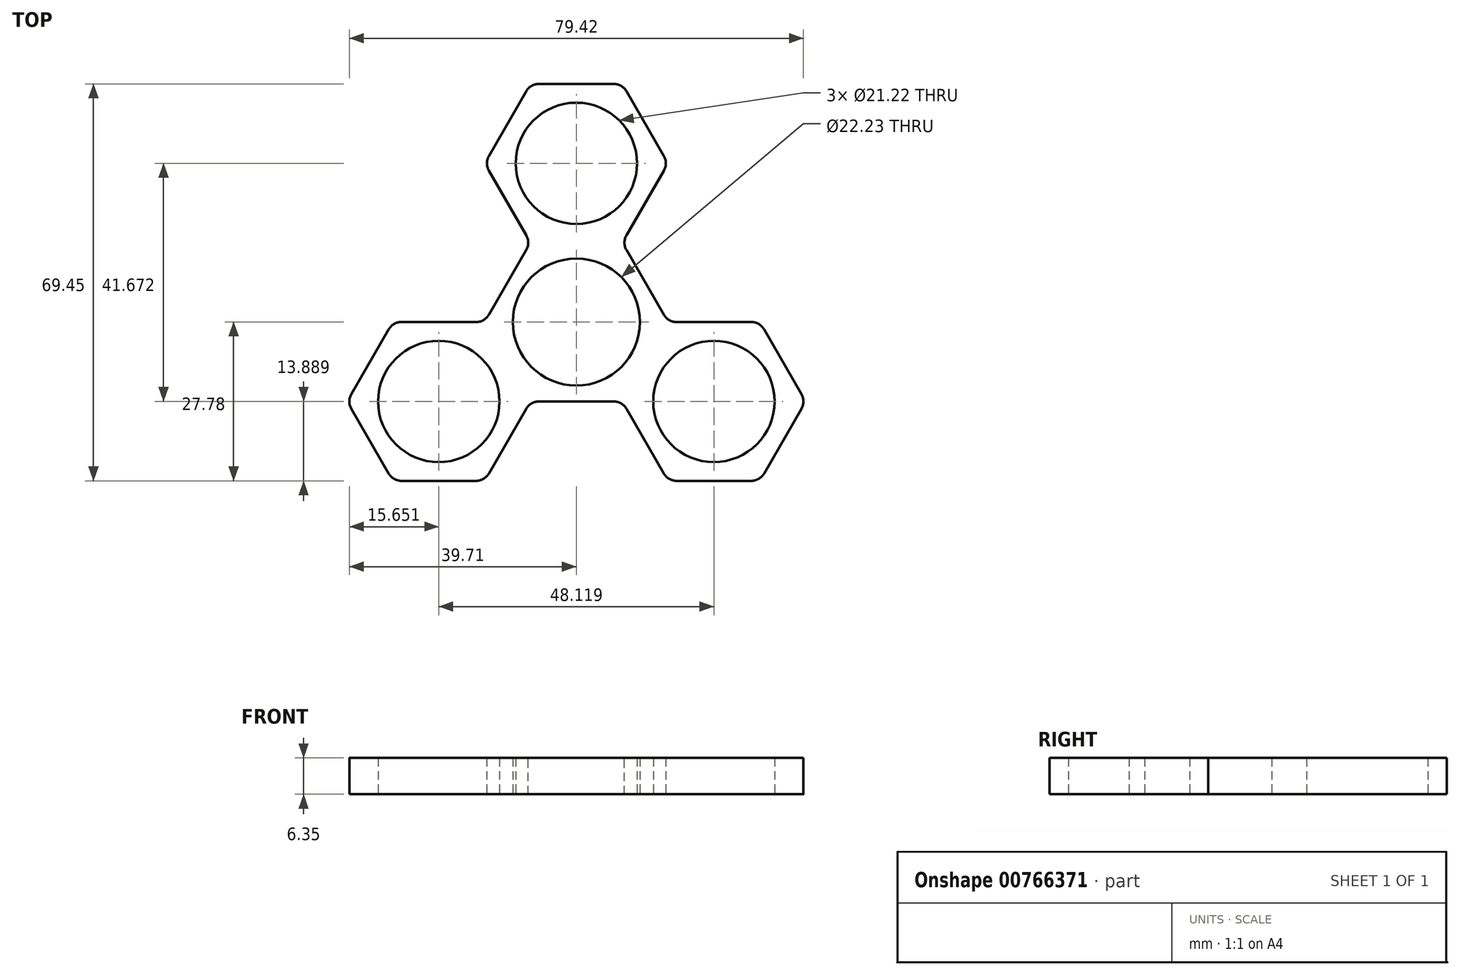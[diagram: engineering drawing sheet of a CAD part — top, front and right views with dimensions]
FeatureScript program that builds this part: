
annotation { "Feature Type Name" : "Feature", "Feature Type Description" : "" }
export const myFeature = defineFeature(function(context is Context, id is Id, definition is map)
    precondition{}
    {
        {
            var Q0;
            Q0=qCreatedBy(makeId("Top.planeOp"),FACE);
            var sketch = newSketch(context, id + "F0", { "sketchPlane" : qUnion([Q0])});
            skCircle(sketch, "E0", {"center": v(0, 0) * mm, "radius": 13.9 * mm});
            skCircle(sketch, "E1.cCircle", {"center": v(0, 0) * mm, "radius": 13.9 * mm, "construction": true});
            skLineSegment(sketch, "E1.0", {"start": v(-8.02, 13.9) * mm, "end": v(8.02, 13.9) * mm});
            skLineSegment(sketch, "E1.1", {"start": v(8.02, 13.9) * mm, "end": v(16.04, 0) * mm});
            skLineSegment(sketch, "E1.2", {"start": v(16.04, 0) * mm, "end": v(8.02, -13.9) * mm});
            skLineSegment(sketch, "E1.3", {"start": v(8.02, -13.9) * mm, "end": v(-8.02, -13.9) * mm});
            skLineSegment(sketch, "E1.4", {"start": v(-8.02, -13.9) * mm, "end": v(-16.04, 0) * mm});
            skLineSegment(sketch, "E1.5", {"start": v(-16.04, 0) * mm, "end": v(-8.02, 13.9) * mm});
            skPoint(sketch, "E1.0.midPoint", {"position": v(0, 13.9) * mm});
            skCircle(sketch, "E2", {"center": v(0, 27.78) * mm, "radius": 13.9 * mm});
            skLineSegment(sketch, "E3.0", {"start": v(8.02, 13.9) * mm, "end": v(-8.02, 13.9) * mm});
            skLineSegment(sketch, "E3.1", {"start": v(-8.02, 13.9) * mm, "end": v(-16.04, 27.78) * mm});
            skLineSegment(sketch, "E3.2", {"start": v(-16.04, 27.78) * mm, "end": v(-8.02, 41.67) * mm});
            skLineSegment(sketch, "E3.3", {"start": v(-8.02, 41.67) * mm, "end": v(8.02, 41.67) * mm});
            skLineSegment(sketch, "E3.4", {"start": v(8.02, 41.67) * mm, "end": v(16.04, 27.78) * mm});
            skLineSegment(sketch, "E3.5", {"start": v(16.04, 27.78) * mm, "end": v(8.02, 13.9) * mm});
            skCircle(sketch, "E4.cCircle", {"center": v(-24.06, -13.9) * mm, "radius": 13.9 * mm, "construction": true});
            skLineSegment(sketch, "E4.0", {"start": v(-16.04, 0) * mm, "end": v(-8.02, -13.9) * mm});
            skLineSegment(sketch, "E4.1", {"start": v(-8.02, -13.9) * mm, "end": v(-16.04, -27.78) * mm});
            skLineSegment(sketch, "E4.2", {"start": v(-16.04, -27.78) * mm, "end": v(-32.08, -27.78) * mm});
            skLineSegment(sketch, "E4.3", {"start": v(-32.08, -27.78) * mm, "end": v(-40.1, -13.9) * mm});
            skLineSegment(sketch, "E4.4", {"start": v(-40.1, -13.9) * mm, "end": v(-32.08, 0) * mm});
            skLineSegment(sketch, "E4.5", {"start": v(-32.08, 0) * mm, "end": v(-16.04, 0) * mm});
            skPoint(sketch, "E4.0.midPoint", {"position": v(-12.03, -6.95) * mm});
            skCircle(sketch, "E5.cCircle", {"center": v(24.06, -13.9) * mm, "radius": 13.9 * mm, "construction": true});
            skLineSegment(sketch, "E5.0", {"start": v(8.02, -13.9) * mm, "end": v(16.04, 0) * mm});
            skLineSegment(sketch, "E5.1", {"start": v(16.04, 0) * mm, "end": v(32.08, 0) * mm});
            skLineSegment(sketch, "E5.2", {"start": v(32.08, 0) * mm, "end": v(40.1, -13.9) * mm});
            skLineSegment(sketch, "E5.3", {"start": v(40.1, -13.9) * mm, "end": v(32.08, -27.78) * mm});
            skLineSegment(sketch, "E5.4", {"start": v(32.08, -27.78) * mm, "end": v(16.04, -27.78) * mm});
            skLineSegment(sketch, "E5.5", {"start": v(16.04, -27.78) * mm, "end": v(8.02, -13.9) * mm});
            skPoint(sketch, "E5.0.midPoint", {"position": v(12.03, -6.95) * mm});
            skCircle(sketch, "E6", {"center": v(-24.06, -13.9) * mm, "radius": 10.6 * mm});
            skCircle(sketch, "E7", {"center": v(0, 0) * mm, "radius": 11.11 * mm});
            skCircle(sketch, "E8", {"center": v(0, 27.78) * mm, "radius": 10.6 * mm});
            skCircle(sketch, "E9", {"center": v(24.06, -13.9) * mm, "radius": 10.6 * mm});
            skSolve(sketch);
        }
        {
            var Q0;
            Q0 = qSketchRegion(id + "F0", true);
            extrude(context, id + "F1", {"entities" : qUnion([Q0]), "depth" : 6.35 * mm, "offsetDistance" : 25.4 * mm});
        }
        {
            var Q0;
            Q0=makeQuery(id+"F1.opExtrude","SWEPT_EDGE",EDGE,{"disambiguationData":[OSD([sQuery(id+"F0.wireOp",EDGE,"E1.3"),sQuery(id+"F0.wireOp",EDGE,"E4.0"),sQuery(id+"F0.wireOp",EDGE,"E4.1")])]});
            var Q1;
            Q1=makeQuery(id+"F1.opExtrude","SWEPT_EDGE",EDGE,{"disambiguationData":[OSD([sQuery(id+"F0.wireOp",EDGE,"E1.3"),sQuery(id+"F0.wireOp",EDGE,"E5.0"),sQuery(id+"F0.wireOp",EDGE,"E5.5")])]});
            var Q2;
            Q2=makeQuery(id+"F1.opExtrude","SWEPT_EDGE",EDGE,{"disambiguationData":[OSD([sQuery(id+"F0.wireOp",EDGE,"E5.4"),sQuery(id+"F0.wireOp",EDGE,"E5.5")])]});
            var Q3;
            Q3=makeQuery(id+"F1.opExtrude","SWEPT_EDGE",EDGE,{"disambiguationData":[OSD([sQuery(id+"F0.wireOp",EDGE,"E5.3"),sQuery(id+"F0.wireOp",EDGE,"E5.4")])]});
            var Q4;
            Q4=makeQuery(id+"F1.opExtrude","SWEPT_EDGE",EDGE,{"disambiguationData":[OSD([sQuery(id+"F0.wireOp",EDGE,"E5.2"),sQuery(id+"F0.wireOp",EDGE,"E5.3")])]});
            var Q5;
            Q5=makeQuery(id+"F1.opExtrude","SWEPT_EDGE",EDGE,{"disambiguationData":[OSD([sQuery(id+"F0.wireOp",EDGE,"E4.1"),sQuery(id+"F0.wireOp",EDGE,"E4.2")])]});
            var Q6;
            Q6=makeQuery(id+"F1.opExtrude","SWEPT_EDGE",EDGE,{"disambiguationData":[OSD([sQuery(id+"F0.wireOp",EDGE,"E4.2"),sQuery(id+"F0.wireOp",EDGE,"E4.3")])]});
            var Q7;
            Q7=makeQuery(id+"F1.opExtrude","SWEPT_EDGE",EDGE,{"disambiguationData":[OSD([sQuery(id+"F0.wireOp",EDGE,"E4.3"),sQuery(id+"F0.wireOp",EDGE,"E4.4")])]});
            var Q8;
            Q8=makeQuery(id+"F1.opExtrude","SWEPT_EDGE",EDGE,{"disambiguationData":[OSD([sQuery(id+"F0.wireOp",EDGE,"E5.1"),sQuery(id+"F0.wireOp",EDGE,"E5.2")])]});
            var Q9;
            Q9=makeQuery(id+"F1.opExtrude","SWEPT_EDGE",EDGE,{"disambiguationData":[OSD([sQuery(id+"F0.wireOp",EDGE,"E1.1"),sQuery(id+"F0.wireOp",EDGE,"E5.0"),sQuery(id+"F0.wireOp",EDGE,"E5.1")])]});
            var Q10;
            Q10=makeQuery(id+"F1.opExtrude","SWEPT_EDGE",EDGE,{"disambiguationData":[OSD([sQuery(id+"F0.wireOp",EDGE,"E3.4"),sQuery(id+"F0.wireOp",EDGE,"E3.5")])]});
            var Q11;
            Q11=makeQuery(id+"F1.opExtrude","SWEPT_EDGE",EDGE,{"disambiguationData":[OSD([sQuery(id+"F0.wireOp",EDGE,"E3.3"),sQuery(id+"F0.wireOp",EDGE,"E3.4")])]});
            var Q12;
            Q12=makeQuery(id+"F1.opExtrude","SWEPT_EDGE",EDGE,{"disambiguationData":[OSD([sQuery(id+"F0.wireOp",EDGE,"E3.2"),sQuery(id+"F0.wireOp",EDGE,"E3.3")])]});
            var Q13;
            Q13=makeQuery(id+"F1.opExtrude","SWEPT_EDGE",EDGE,{"disambiguationData":[OSD([sQuery(id+"F0.wireOp",EDGE,"E1.1"),sQuery(id+"F0.wireOp",EDGE,"E3.0"),sQuery(id+"F0.wireOp",EDGE,"E3.5")])]});
            var Q14;
            Q14=makeQuery(id+"F1.opExtrude","SWEPT_EDGE",EDGE,{"disambiguationData":[OSD([sQuery(id+"F0.wireOp",EDGE,"E3.1"),sQuery(id+"F0.wireOp",EDGE,"E3.2")])]});
            var Q15;
            Q15=makeQuery(id+"F1.opExtrude","SWEPT_EDGE",EDGE,{"disambiguationData":[OSD([sQuery(id+"F0.wireOp",EDGE,"E1.5"),sQuery(id+"F0.wireOp",EDGE,"E3.0"),sQuery(id+"F0.wireOp",EDGE,"E3.1")])]});
            var Q16;
            Q16=makeQuery(id+"F1.opExtrude","SWEPT_EDGE",EDGE,{"disambiguationData":[OSD([sQuery(id+"F0.wireOp",EDGE,"E1.5"),sQuery(id+"F0.wireOp",EDGE,"E4.0"),sQuery(id+"F0.wireOp",EDGE,"E4.5")])]});
            var Q17;
            Q17=makeQuery(id+"F1.opExtrude","SWEPT_EDGE",EDGE,{"disambiguationData":[OSD([sQuery(id+"F0.wireOp",EDGE,"E4.4"),sQuery(id+"F0.wireOp",EDGE,"E4.5")])]});
            fillet(context, id + "F2", {"entities" : qUnion([Q0, Q1, Q2, Q3, Q4, Q5, Q6, Q7, Q8, Q9, Q10, Q11, Q12, Q13, Q14, Q15, Q16, Q17]), "radius" : 2.54 * mm, "tangentPropagation" : true, "allowEdgeOverflow" : false});
        }
    });
